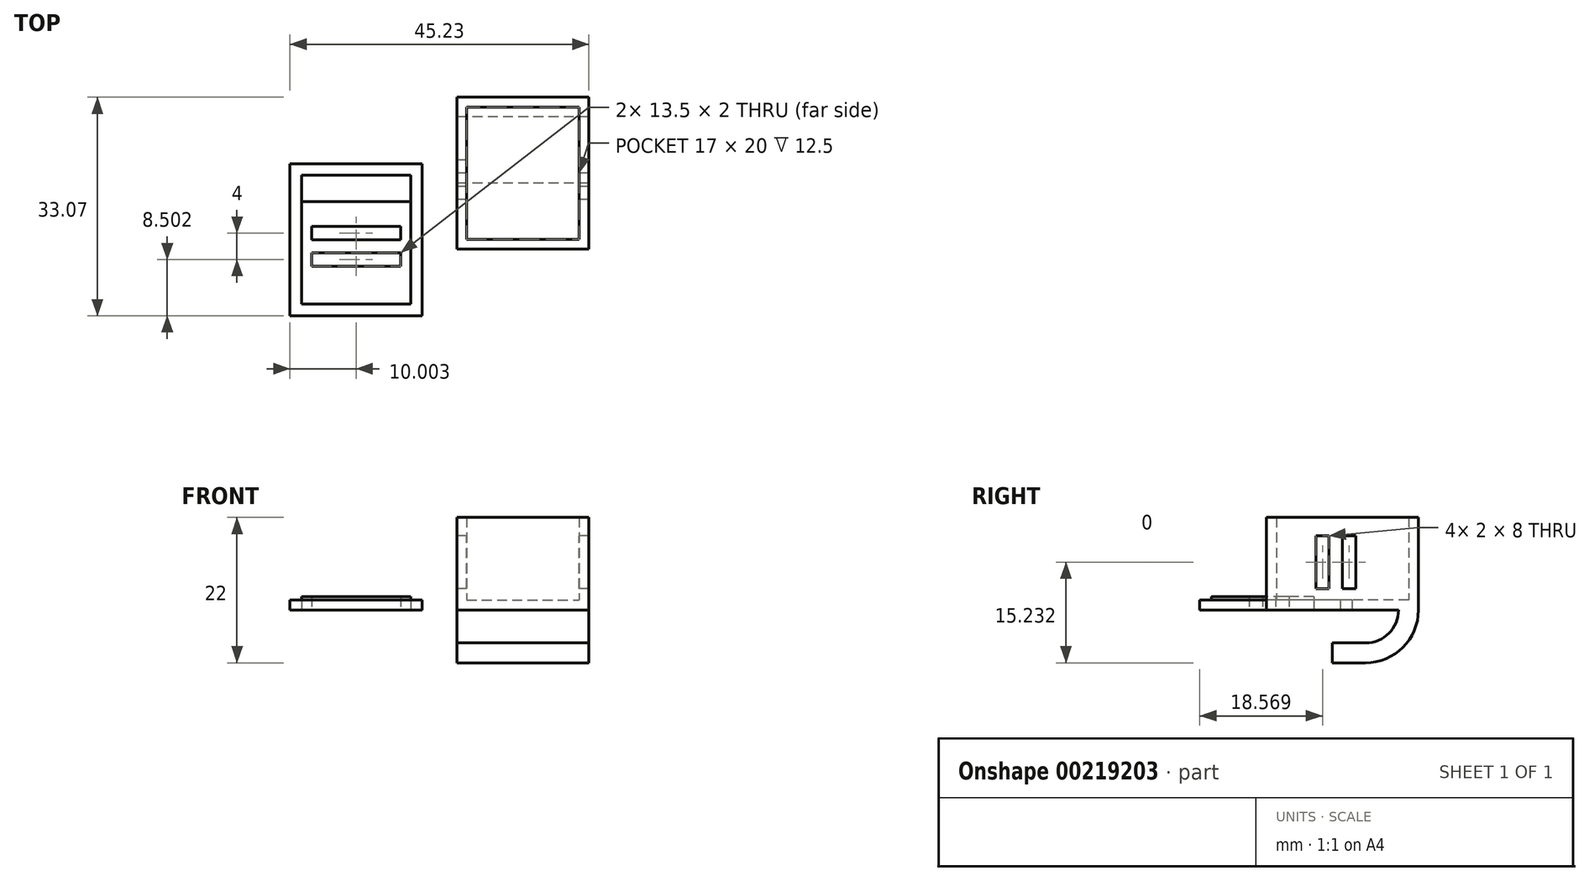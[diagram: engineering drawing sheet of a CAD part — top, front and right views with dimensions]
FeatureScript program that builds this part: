
annotation { "Feature Type Name" : "Feature", "Feature Type Description" : "" }
export const myFeature = defineFeature(function(context is Context, id is Id, definition is map)
    precondition{}
    {
        {
            var Q0;
            Q0=qCreatedBy(makeId("Top.planeOp"),FACE);
            var sketch = newSketch(context, id + "F0", { "sketchPlane" : qUnion([Q0])});
            skLineSegment(sketch, "E0.bottom", {"start": v(-8.78, 6.45) * mm, "end": v(8.22, 6.45) * mm});
            skLineSegment(sketch, "E0.top", {"start": v(-8.78, -13.55) * mm, "end": v(8.22, -13.55) * mm});
            skLineSegment(sketch, "E0.left", {"start": v(-8.78, 6.45) * mm, "end": v(-8.78, -13.55) * mm});
            skLineSegment(sketch, "E0.right", {"start": v(8.22, 6.45) * mm, "end": v(8.22, -13.55) * mm});
            skLineSegment(sketch, "E1.bottom", {"start": v(-10.28, 7.95) * mm, "end": v(9.72, 7.95) * mm});
            skLineSegment(sketch, "E1.top", {"start": v(-10.28, -15.05) * mm, "end": v(9.72, -15.05) * mm});
            skLineSegment(sketch, "E1.left", {"start": v(-10.28, 7.95) * mm, "end": v(-10.28, -15.05) * mm});
            skLineSegment(sketch, "E1.right", {"start": v(9.72, 7.95) * mm, "end": v(9.72, -15.05) * mm});
            skSolve(sketch);
        }
        {
            var Q0;
            Q0=makeQuery(id+"F0.imprint","IMPRINT",FACE,{"disambiguationData":[TD([[makeQuery(id+"F0.imprint","IMPRINT",EDGE,{"derivedFrom":sQuery(id+"F0.wireOp",EDGE,"E0.bottom")}),1.0]])]});
            extrude(context, id + "F1", {"entities" : qUnion([Q0]), "depth" : 14 * mm});
        }
        {
            var Q0;
            Q0=makeQuery(id+"F0.imprint","IMPRINT",FACE,{"disambiguationData":[TD([[makeQuery(id+"F0.imprint","IMPRINT",EDGE,{"derivedFrom":sQuery(id+"F0.wireOp",EDGE,"E0.bottom")}),-1.0]])]});
            extrude(context, id + "F2", {"entities" : qUnion([Q0]), "operationType" : NewBodyOperationType.ADD, "depth" : 1.5 * mm});
        }
        {
            var Q0;
            Q0=qCreatedBy(makeId("Top.planeOp"),FACE);
            var sketch = newSketch(context, id + "F3", { "sketchPlane" : qUnion([Q0])});
            skLineSegment(sketch, "E2.bottom", {"start": v(-33.76, -3.87) * mm, "end": v(-17.26, -3.87) * mm});
            skLineSegment(sketch, "E2.top", {"start": v(-33.76, -23.37) * mm, "end": v(-17.26, -23.37) * mm});
            skLineSegment(sketch, "E2.left", {"start": v(-33.76, -3.87) * mm, "end": v(-33.76, -23.37) * mm});
            skLineSegment(sketch, "E2.right", {"start": v(-17.26, -3.87) * mm, "end": v(-17.26, -23.37) * mm});
            skLineSegment(sketch, "E3.bottom", {"start": v(-35.5, -2.12) * mm, "end": v(-15.5, -2.12) * mm});
            skLineSegment(sketch, "E3.top", {"start": v(-35.5, -25.12) * mm, "end": v(-15.5, -25.12) * mm});
            skLineSegment(sketch, "E3.left", {"start": v(-35.5, -2.12) * mm, "end": v(-35.5, -25.12) * mm});
            skLineSegment(sketch, "E3.right", {"start": v(-15.5, -2.12) * mm, "end": v(-15.5, -25.12) * mm});
            skLineSegment(sketch, "E4.top", {"start": v(-33.76, -7.87) * mm, "end": v(-17.26, -7.87) * mm});
            skLineSegment(sketch, "E4.left", {"start": v(-33.76, -3.87) * mm, "end": v(-33.76, -7.87) * mm});
            skLineSegment(sketch, "E4.right", {"start": v(-17.26, -3.87) * mm, "end": v(-17.26, -7.87) * mm});
            skLineSegment(sketch, "E5.bottom", {"start": v(-32.26, -11.62) * mm, "end": v(-18.76, -11.62) * mm});
            skLineSegment(sketch, "E5.top", {"start": v(-32.26, -13.62) * mm, "end": v(-18.76, -13.62) * mm});
            skLineSegment(sketch, "E5.left", {"start": v(-32.26, -11.62) * mm, "end": v(-32.26, -13.62) * mm});
            skLineSegment(sketch, "E5.right", {"start": v(-18.76, -11.62) * mm, "end": v(-18.76, -13.62) * mm});
            skLineSegment(sketch, "E6.bottom", {"start": v(-32.26, -15.62) * mm, "end": v(-18.76, -15.62) * mm});
            skLineSegment(sketch, "E6.top", {"start": v(-32.26, -17.62) * mm, "end": v(-18.76, -17.62) * mm});
            skLineSegment(sketch, "E6.left", {"start": v(-32.26, -15.62) * mm, "end": v(-32.26, -17.62) * mm});
            skLineSegment(sketch, "E6.right", {"start": v(-18.76, -15.62) * mm, "end": v(-18.76, -17.62) * mm});
            skSolve(sketch);
        }
        {
            var Q0;
            Q0 = qSketchRegion(id + "F3", true);
            extrude(context, id + "F4", {"entities" : qUnion([Q0]), "depth" : 1.5 * mm});
        }
        {
            var Q0;
            Q0=makeQuery(id+"F3.imprint","IMPRINT",FACE,{"disambiguationData":[TD([[makeQuery(id+"F3.imprint","IMPRINT",EDGE,{"derivedFrom":sQuery(id+"F3.wireOp",EDGE,"E2.top")}),1.0]])]});
            extrude(context, id + "F5", {"entities" : qUnion([Q0]), "operationType" : NewBodyOperationType.ADD, "depth" : 2 * mm});
        }
        {
            var Q0;
            Q0=makeQuery(id+"F1.opExtrude","SWEPT_FACE",FACE,{"disambiguationData":[OSD([sQuery(id+"F0.wireOp",EDGE,"E1.left")])]});
            var sketch = newSketch(context, id + "F6", { "sketchPlane" : qUnion([Q0])});
            skLineSegment(sketch, "E7.bottom", {"start": v(1.55, 11.23) * mm, "end": v(3.55, 11.23) * mm});
            skLineSegment(sketch, "E7.top", {"start": v(1.55, 3.23) * mm, "end": v(3.55, 3.23) * mm});
            skLineSegment(sketch, "E7.left", {"start": v(1.55, 11.23) * mm, "end": v(1.55, 3.23) * mm});
            skLineSegment(sketch, "E7.right", {"start": v(3.55, 11.23) * mm, "end": v(3.55, 3.23) * mm});
            skLineSegment(sketch, "E8.bottom", {"start": v(5.55, 11.23) * mm, "end": v(7.55, 11.23) * mm});
            skLineSegment(sketch, "E8.top", {"start": v(5.55, 3.23) * mm, "end": v(7.55, 3.23) * mm});
            skLineSegment(sketch, "E8.left", {"start": v(5.55, 11.23) * mm, "end": v(5.55, 3.23) * mm});
            skLineSegment(sketch, "E8.right", {"start": v(7.55, 11.23) * mm, "end": v(7.55, 3.23) * mm});
            skSolve(sketch);
        }
        {
            var Q0;
            Q0=makeQuery(id+"F6.imprint","IMPRINT",FACE,{"disambiguationData":[TD([[makeQuery(id+"F6.imprint","IMPRINT",EDGE,{"derivedFrom":sQuery(id+"F6.wireOp",EDGE,"E7.bottom")}),-1.0]])]});
            var Q1;
            Q1=makeQuery(id+"F6.imprint","IMPRINT",FACE,{"disambiguationData":[TD([[makeQuery(id+"F6.imprint","IMPRINT",EDGE,{"derivedFrom":sQuery(id+"F6.wireOp",EDGE,"E8.bottom")}),-1.0]])]});
            var Q2;
            Q2=makeQuery(id+"F6.imprint","IMPRINT",FACE,{"disambiguationData":[TD([[makeQuery(id+"F6.imprint","IMPRINT",EDGE,{"derivedFrom":sQuery(id+"F6.wireOp",EDGE,"Cq2O0Xz6-i8tC-OJ7v-Lk0E-LR6c2VhS4r3j.bottom")}),-1.0]])]});
            extrude(context, id + "F7", {"entities" : qUnion([Q0, Q1, Q2]), "operationType" : NewBodyOperationType.REMOVE, "oppositeDirection" : true, "depth" : 25 * mm});
        }
        {
            var Q0;
            Q0=makeQuery(id+"F1.opExtrude","SWEPT_FACE",FACE,{"disambiguationData":[OSD([sQuery(id+"F0.wireOp",EDGE,"E1.left")])]});
            var sketch = newSketch(context, id + "F8", { "sketchPlane" : qUnion([Q0])});
            skArc(sketch, "E9", {"start": v(-4.95, 0) * mm, "mid": v(-3.48, -3.54) * mm, "end": v(0.05, -5) * mm});
            skArc(sketch, "E10", {"start": v(-7.95, 0) * mm, "mid": v(-5.6, -5.66) * mm, "end": v(0.05, -8) * mm});
            skLineSegment(sketch, "E11", {"start": v(0.05, -8) * mm, "end": v(0.05, -5) * mm});
            skLineSegment(sketch, "E12", {"start": v(-7.95, 0) * mm, "end": v(-4.95, 0) * mm});
            skLineSegment(sketch, "E13", {"start": v(0.05, -5) * mm, "end": v(5.05, -5) * mm});
            skLineSegment(sketch, "E14", {"start": v(5.05, -5) * mm, "end": v(5.05, -8) * mm});
            skLineSegment(sketch, "E15", {"start": v(5.05, -8) * mm, "end": v(0.05, -8) * mm});
            skSolve(sketch);
        }
        {
            var Q0;
            Q0=makeQuery(id+"F8.imprint","IMPRINT",FACE,{"disambiguationData":[TD([[makeQuery(id+"F8.imprint","IMPRINT",EDGE,{"derivedFrom":sQuery(id+"F8.wireOp",EDGE,"E9")}),-1.0]])]});
            var Q1;
            Q1=makeQuery(id+"F8.imprint","IMPRINT",FACE,{"disambiguationData":[TD([[makeQuery(id+"F8.imprint","IMPRINT",EDGE,{"derivedFrom":sQuery(id+"F8.wireOp",EDGE,"E11")}),-1.0]])]});
            extrude(context, id + "F9", {"entities" : qUnion([Q0, Q1]), "operationType" : NewBodyOperationType.ADD, "oppositeDirection" : true, "depth" : 20 * mm});
        }
    });
